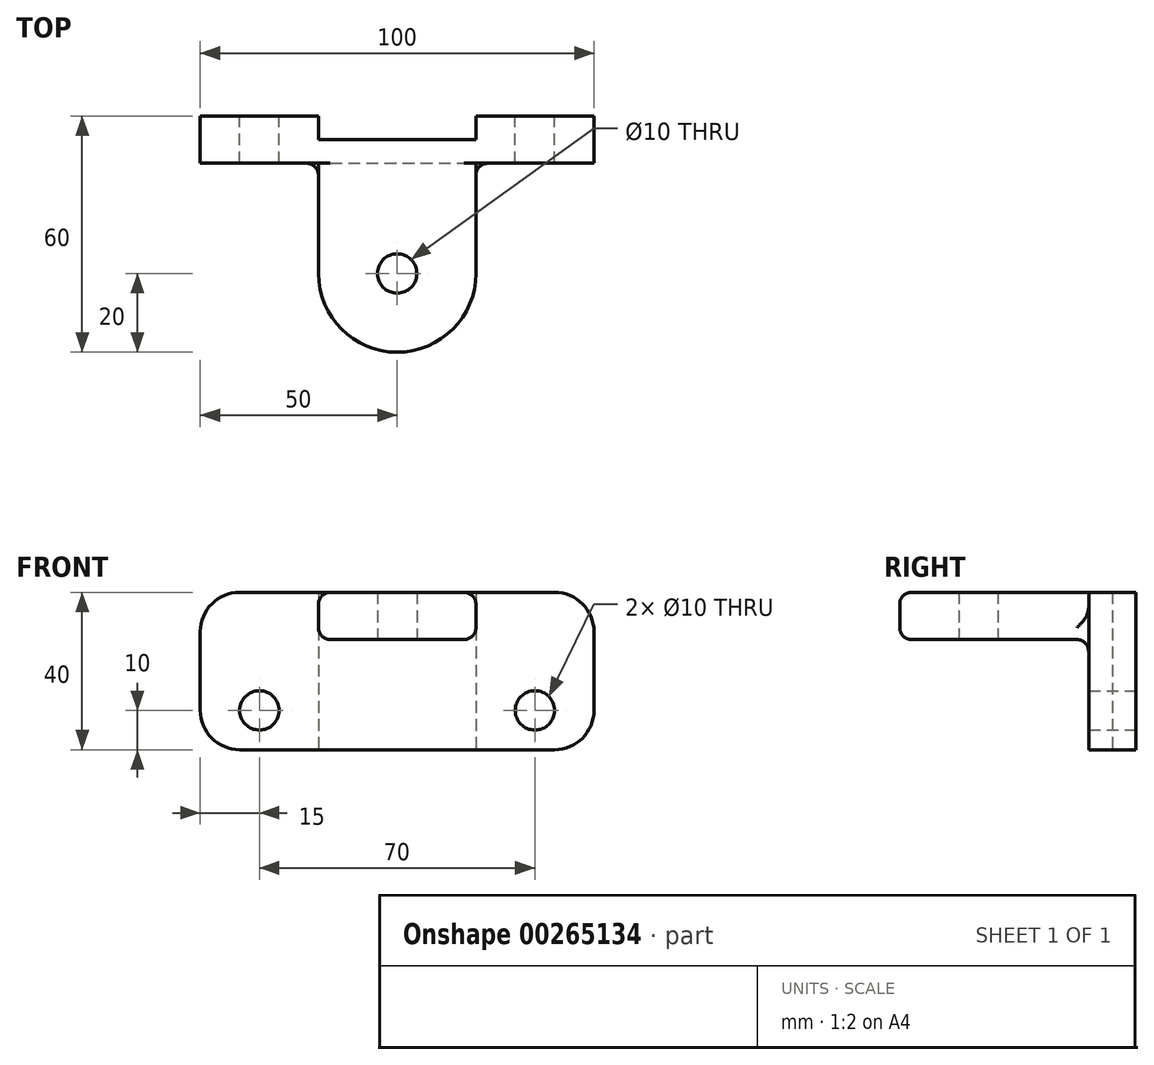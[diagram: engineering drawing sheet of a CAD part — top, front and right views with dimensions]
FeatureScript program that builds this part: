
annotation { "Feature Type Name" : "Feature", "Feature Type Description" : "" }
export const myFeature = defineFeature(function(context is Context, id is Id, definition is map)
    precondition{}
    {
        {
            var Q0;
            Q0=qCreatedBy(makeId("Front.planeOp"),FACE);
            var sketch = newSketch(context, id + "F0", { "sketchPlane" : qUnion([Q0])});
            skLineSegment(sketch, "E0.bottom", {"start": v(-40, 20) * mm, "end": v(40, 20) * mm});
            skLineSegment(sketch, "E0.top", {"start": v(-40, -20) * mm, "end": v(40, -20) * mm});
            skLineSegment(sketch, "E0.left", {"start": v(-50, 10) * mm, "end": v(-50, -10) * mm});
            skLineSegment(sketch, "E0.right", {"start": v(50, 10) * mm, "end": v(50, -10) * mm});
            skPoint(sketch, "E0.middle", {"position": v(0, 0) * mm});
            skArc(sketch, "E1", {"start": v(-40, 20) * mm, "mid": v(-47.07, 17.07) * mm, "end": v(-50, 10) * mm});
            skArc(sketch, "E2.MirrorCS", {"start": v(40, 20) * mm, "mid": v(47.07, 17.07) * mm, "end": v(50, 10) * mm});
            skArc(sketch, "E3.MirrorCS", {"start": v(-40, -20) * mm, "mid": v(-47.07, -17.07) * mm, "end": v(-50, -10) * mm});
            skArc(sketch, "E4.MirrorCS", {"start": v(40, -20) * mm, "mid": v(47.07, -17.07) * mm, "end": v(50, -10) * mm});
            skCircle(sketch, "E5", {"center": v(-35, -10) * mm, "radius": 5 * mm});
            skCircle(sketch, "E6.MirrorC", {"center": v(35, -10) * mm, "radius": 5 * mm});
            skSolve(sketch);
        }
        {
            var Q0;
            Q0=makeQuery(id+"F0.imprint","IMPRINT",FACE,{"disambiguationData":[TD([[makeQuery(id+"F0.imprint","IMPRINT",EDGE,{"derivedFrom":sQuery(id+"F0.wireOp",EDGE,"E0.bottom")}),-1.0]])]});
            extrude(context, id + "F1", {"entities" : qUnion([Q0]), "depth" : 12 * mm});
        }
        {
            var Q0;
            Q0=qCreatedBy(makeId("Front.planeOp"),FACE);
            var sketch = newSketch(context, id + "F2", { "sketchPlane" : qUnion([Q0])});
            skLineSegment(sketch, "E7.bottom", {"start": v(-20, 20) * mm, "end": v(20, 20) * mm});
            skLineSegment(sketch, "E7.top", {"start": v(-20, -20) * mm, "end": v(20, -20) * mm});
            skLineSegment(sketch, "E7.left", {"start": v(-20, 20) * mm, "end": v(-20, -20) * mm});
            skLineSegment(sketch, "E7.right", {"start": v(20, 20) * mm, "end": v(20, -20) * mm});
            skPoint(sketch, "E7.middle", {"position": v(0, 0) * mm});
            skSolve(sketch);
        }
        {
            var Q0;
            Q0 = qSketchRegion(id + "F2", true);
            extrude(context, id + "F3", {"entities" : qUnion([Q0]), "operationType" : NewBodyOperationType.REMOVE, "depth" : 6 * mm});
        }
        {
            var Q0;
            Q0=makeQuery(id+"F1.opExtrude","CAP_FACE",FACE,{"disambiguationData":[OSD([sQuery(id+"F0.wireOp",EDGE,"E0.bottom"),sQuery(id+"F0.wireOp",EDGE,"E0.top"),sQuery(id+"F0.wireOp",EDGE,"E0.left"),sQuery(id+"F0.wireOp",EDGE,"E0.right"),sQuery(id+"F0.wireOp",EDGE,"E1"),sQuery(id+"F0.wireOp",EDGE,"E2.MirrorCS"),sQuery(id+"F0.wireOp",EDGE,"E3.MirrorCS"),sQuery(id+"F0.wireOp",EDGE,"E4.MirrorCS"),sQuery(id+"F0.wireOp",EDGE,"E5"),sQuery(id+"F0.wireOp",EDGE,"E6.MirrorC")])],"isStart":false});
            var sketch = newSketch(context, id + "F4", { "sketchPlane" : qUnion([Q0])});
            skLineSegment(sketch, "E8.bottom", {"start": v(-20, 20) * mm, "end": v(20, 20) * mm});
            skLineSegment(sketch, "E8.top", {"start": v(-20, 8) * mm, "end": v(20, 8) * mm});
            skLineSegment(sketch, "E8.left", {"start": v(-20, 20) * mm, "end": v(-20, 8) * mm});
            skLineSegment(sketch, "E8.right", {"start": v(20, 20) * mm, "end": v(20, 8) * mm});
            skSolve(sketch);
        }
        {
            var Q0;
            Q0=makeQuery(id+"F4.imprint","IMPRINT",FACE,{"disambiguationData":[TD([[makeQuery(id+"F4.imprint","IMPRINT",EDGE,{"derivedFrom":sQuery(id+"F4.wireOp",EDGE,"E8.bottom")}),-1.0]])]});
            extrude(context, id + "F5", {"entities" : qUnion([Q0]), "operationType" : NewBodyOperationType.ADD, "depth" : 28 * mm});
        }
        {
            var Q0;
            Q0=makeQuery(id+"F5.boolean.opBoolean","MERGE",FACE,{"derivedFrom":[makeQuery(id+"F1.opExtrude","SWEPT_FACE",FACE,{"disambiguationData":[OSD([sQuery(id+"F0.wireOp",EDGE,"E0.bottom")])]}),makeQuery(id+"F5.opExtrude","SWEPT_FACE",FACE,{"disambiguationData":[OSD([sQuery(id+"F4.wireOp",EDGE,"E8.bottom")])]})]});
            var sketch = newSketch(context, id + "F6", { "sketchPlane" : qUnion([Q0])});
            skArc(sketch, "E9", {"start": v(-20, -40) * mm, "mid": v(0, -60) * mm, "end": v(20, -40) * mm});
            skSolve(sketch);
        }
        {
            var Q0;
            Q0=makeQuery(id+"F6.imprint","IMPRINT",FACE,{"disambiguationData":[TD([[makeQuery(id+"F6.imprint","IMPRINT",EDGE,{"derivedFrom":sQuery(id+"F6.wireOp",EDGE,"E9")}),1.0]])]});
            extrude(context, id + "F7", {"entities" : qUnion([Q0]), "operationType" : NewBodyOperationType.ADD, "oppositeDirection" : true, "depth" : 12 * mm});
        }
        {
            var Q0;
            Q0=makeQuery(id+"F7.boolean.opBoolean","MERGE",FACE,{"derivedFrom":[makeQuery(id+"F5.opExtrude","SWEPT_FACE",FACE,{"disambiguationData":[OSD([sQuery(id+"F4.wireOp",EDGE,"E8.top")])]}),makeQuery(id+"F7.opExtrude","CAP_FACE",FACE,{"disambiguationData":[OSD([sQuery(id+"F4.wireOp",EDGE,"E8.bottom"),sQuery(id+"F6.wireOp",EDGE,"E9")])],"isStart":false})]});
            var Q1;
            Q1=makeQuery(id+"F5.opExtrude","CAP_EDGE",EDGE,{"disambiguationData":[OSD([sQuery(id+"F4.wireOp",EDGE,"E8.top")])],"isStart":true});
            fillet(context, id + "F8", {"entities" : qUnion([Q0, Q1]), "radius" : 3 * mm, "tangentPropagation" : true, "allowEdgeOverflow" : false});
        }
        {
            var Q0;
            Q0=makeQuery(id+"F7.opExtrude","SWEPT_FACE",FACE,{"disambiguationData":[OSD([sQuery(id+"F6.wireOp",EDGE,"E9")])]});
            fillet(context, id + "F9", {"entities" : qUnion([Q0]), "radius" : 3 * mm, "tangentPropagation" : true, "allowEdgeOverflow" : false});
        }
        {
            var Q0;
            Q0=makeQuery(id+"F7.boolean.opBoolean","MERGE",FACE,{"derivedFrom":[makeQuery(id+"F5.opExtrude","SWEPT_FACE",FACE,{"disambiguationData":[OSD([sQuery(id+"F4.wireOp",EDGE,"E8.top")])]}),makeQuery(id+"F7.opExtrude","CAP_FACE",FACE,{"disambiguationData":[OSD([sQuery(id+"F4.wireOp",EDGE,"E8.bottom"),sQuery(id+"F6.wireOp",EDGE,"E9")])],"isStart":false})]});
            var sketch = newSketch(context, id + "F10", { "sketchPlane" : qUnion([Q0])});
            skCircle(sketch, "E10", {"center": v(0, 40) * mm, "radius": 5 * mm});
            skSolve(sketch);
        }
        {
            var Q0;
            Q0=makeQuery(id+"F10.imprint","IMPRINT",FACE,{"disambiguationData":[TD([[makeQuery(id+"F10.imprint","IMPRINT",EDGE,{"derivedFrom":sQuery(id+"F10.wireOp",EDGE,"E10")}),1.0]])]});
            extrude(context, id + "F11", {"entities" : qUnion([Q0]), "operationType" : NewBodyOperationType.REMOVE, "oppositeDirection" : true, "depth" : 25 * mm});
        }
    });
